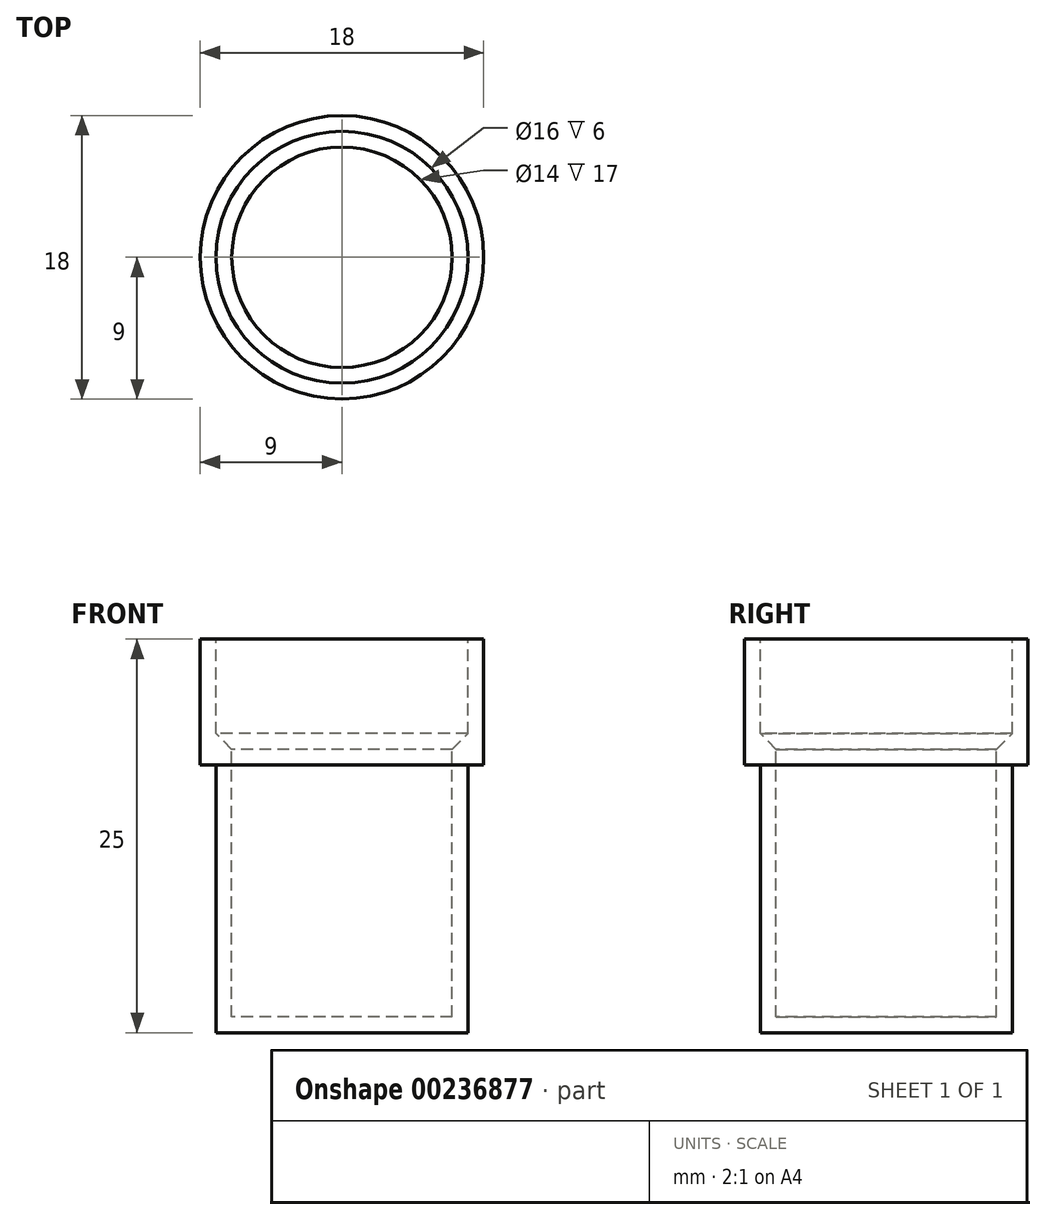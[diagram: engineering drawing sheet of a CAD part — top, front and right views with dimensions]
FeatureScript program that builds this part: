
annotation { "Feature Type Name" : "Feature", "Feature Type Description" : "" }
export const myFeature = defineFeature(function(context is Context, id is Id, definition is map)
    precondition{}
    {
        {
            var Q0;
            Q0=qCreatedBy(makeId("Front.planeOp"),FACE);
            var sketch = newSketch(context, id + "F0", { "sketchPlane" : qUnion([Q0])});
            skLineSegment(sketch, "E0", {"start": v(8, 0) * mm, "end": v(8, -6) * mm});
            skLineSegment(sketch, "E1", {"start": v(8, -6) * mm, "end": v(7, -7) * mm});
            skLineSegment(sketch, "E2", {"start": v(7, -7) * mm, "end": v(7, -24) * mm});
            skLineSegment(sketch, "E3", {"start": v(7, -24) * mm, "end": v(0, -24) * mm});
            skLineSegment(sketch, "E4", {"start": v(0, -24) * mm, "end": v(0, -25) * mm});
            skLineSegment(sketch, "E5", {"start": v(0, -25) * mm, "end": v(8, -25) * mm});
            skLineSegment(sketch, "E6", {"start": v(9, -7) * mm, "end": v(9, 0) * mm});
            skLineSegment(sketch, "E7", {"start": v(9, 0) * mm, "end": v(8, 0) * mm});
            skLineSegment(sketch, "E8", {"start": v(8, -25) * mm, "end": v(8, -8) * mm});
            skLineSegment(sketch, "E9", {"start": v(8, -8) * mm, "end": v(9, -8) * mm});
            skLineSegment(sketch, "E10", {"start": v(9, -8) * mm, "end": v(9, -7) * mm});
            skSolve(sketch);
        }
        {
            var Q0;
            Q0 = qSketchRegion(id + "F0", true);
            var Q1;
            Q1=sQuery(id+"F0.wireOp",EDGE,"E4");
            revolve(context, id + "F1", {"surfaceOperationType" : NewSurfaceOperationType.NEW, "entities" : qUnion([Q0]), "axis" : qUnion([Q1]), "revolveType" : RevolveType.FULL});
        }
    });
